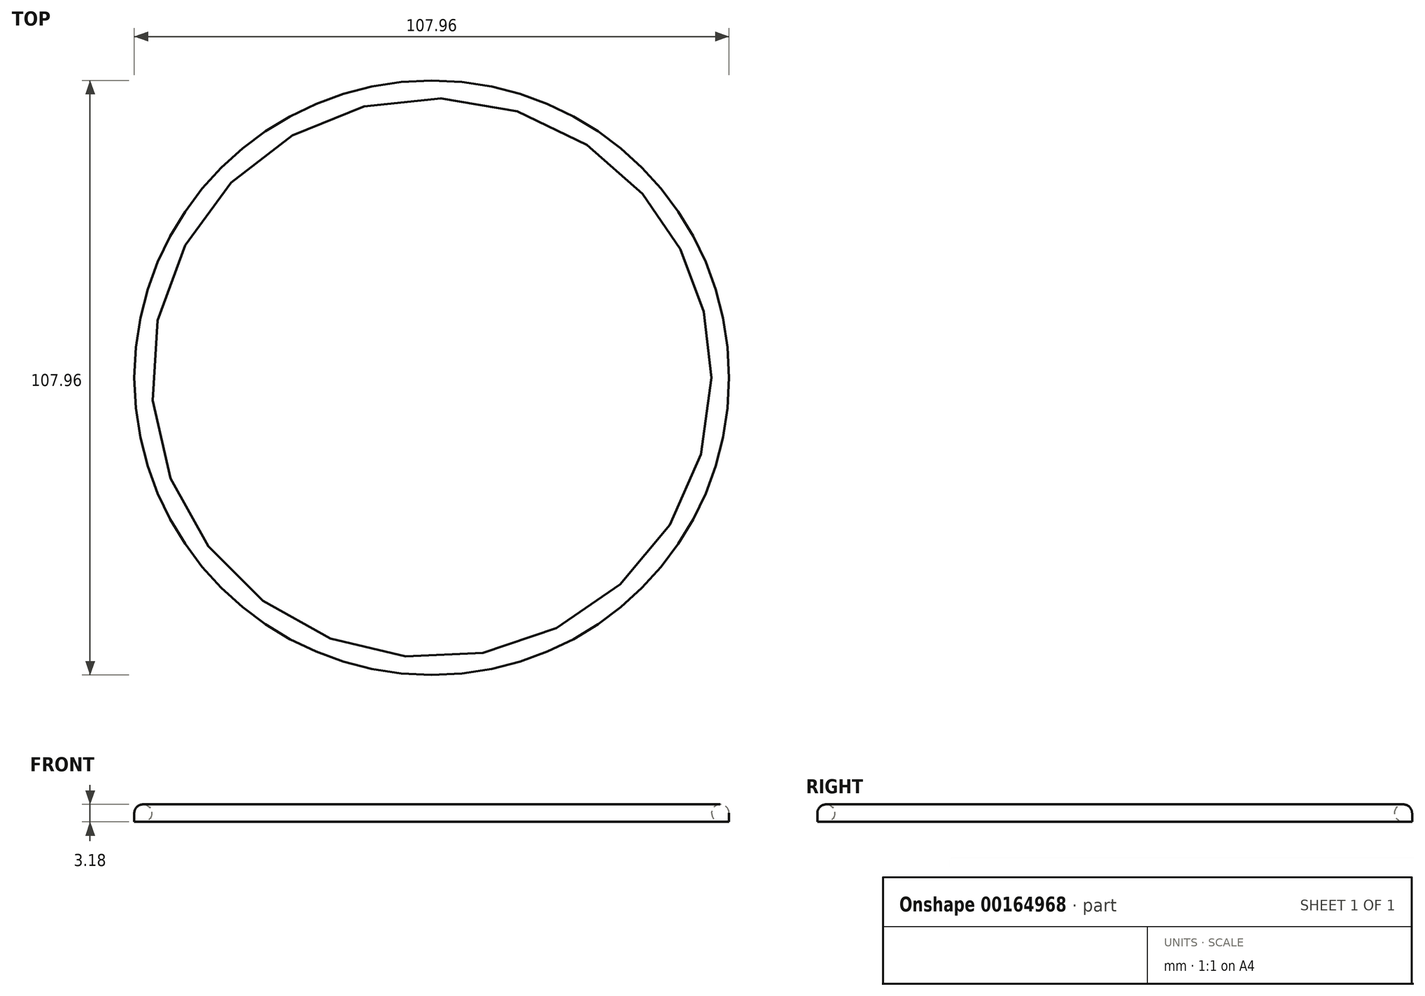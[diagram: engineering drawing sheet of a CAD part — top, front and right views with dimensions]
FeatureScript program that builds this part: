
annotation { "Feature Type Name" : "Feature", "Feature Type Description" : "" }
export const myFeature = defineFeature(function(context is Context, id is Id, definition is map)
    precondition{}
    {
        {
            var Q0;
            Q0=qCreatedBy(makeId("Top.planeOp"),FACE);
            var sketch = newSketch(context, id + "F0", { "sketchPlane" : qUnion([Q0])});
            skCircle(sketch, "E0", {"center": v(0, 0) * mm, "radius": 50.8 * mm});
            skCircle(sketch, "E1", {"center": v(0, 0) * mm, "radius": 53.98 * mm});
            skSolve(sketch);
        }
        {
            var Q0;
            Q0=qSketchRegion(id+"F0",true);
            extrude(context, id + "F1", {"entities" : qUnion([Q0]), "depth" : 3.17 * mm});
        }
        {
            var Q0;
            Q0=makeQuery(id+"F1.opExtrude","CAP_EDGE",EDGE,{"disambiguationData":[OSD([sQuery(id+"F0.wireOp",EDGE,"E0")])],"isStart":false});
            var Q1;
            Q1=makeQuery(id+"F1.opExtrude","CAP_EDGE",EDGE,{"disambiguationData":[OSD([sQuery(id+"F0.wireOp",EDGE,"E1")])],"isStart":false});
            var Q2;
            Q2=makeQuery(id+"F1.opExtrude","CAP_EDGE",EDGE,{"disambiguationData":[OSD([sQuery(id+"F0.wireOp",EDGE,"E0")])],"isStart":true});
            fillet(context, id + "F2", {"entities" : qUnion([Q0, Q1, Q2]), "radius" : 1.59 * mm, "tangentPropagation" : true, "allowEdgeOverflow" : false});
        }
    });
